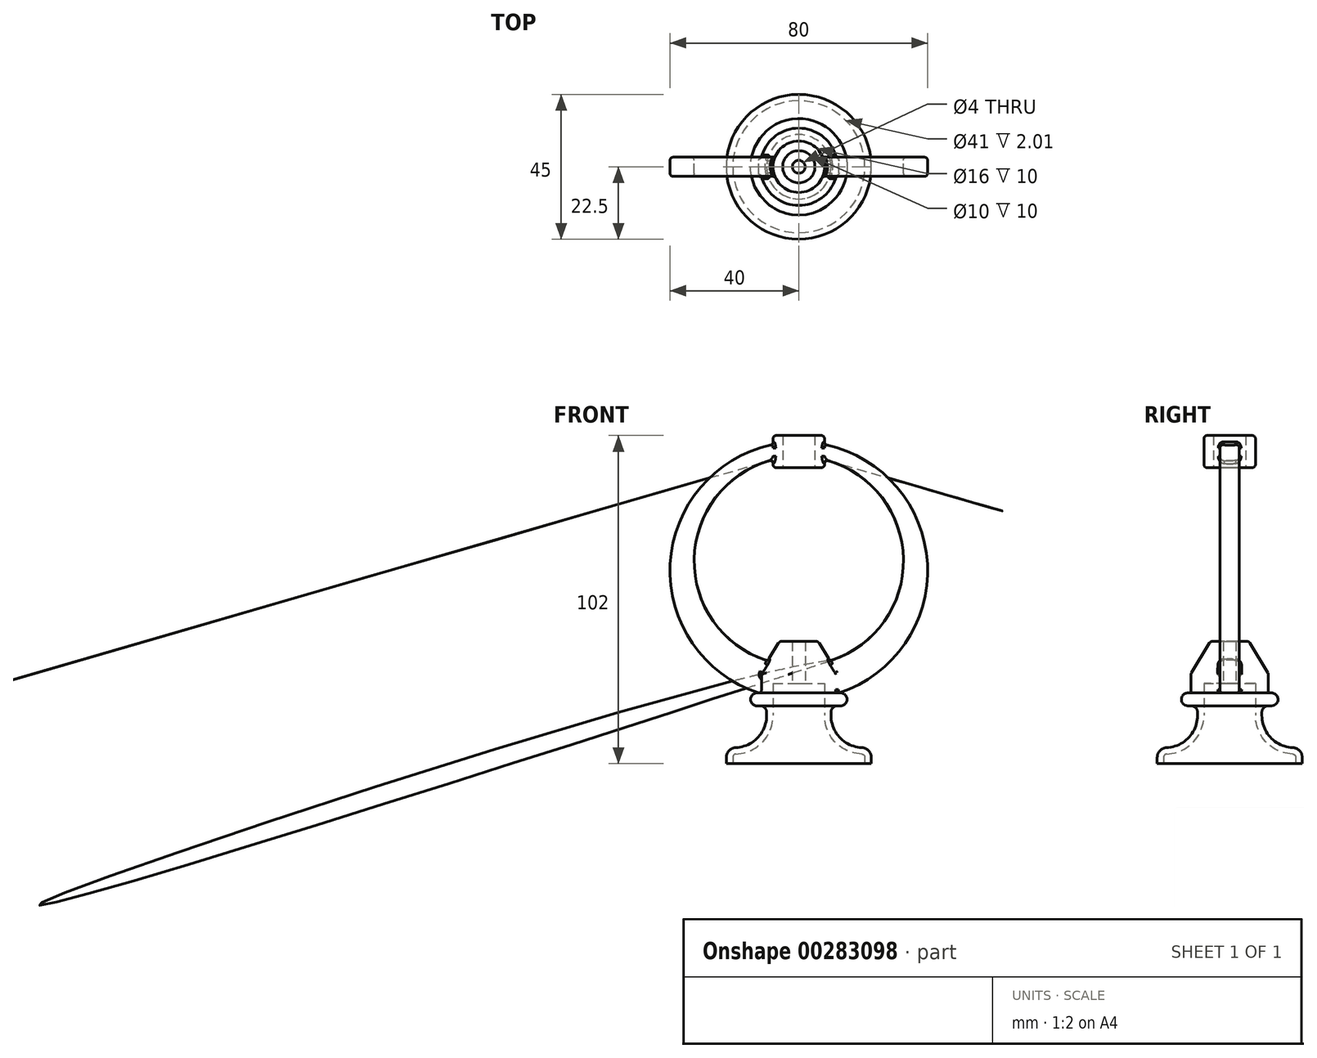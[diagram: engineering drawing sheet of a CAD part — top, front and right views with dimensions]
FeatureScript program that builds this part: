
annotation { "Feature Type Name" : "Feature", "Feature Type Description" : "" }
export const myFeature = defineFeature(function(context is Context, id is Id, definition is map)
    precondition{}
    {
        {
            var Q0;
            Q0=qCreatedBy(makeId("Front.planeOp"),FACE);
            var sketch = newSketch(context, id + "F0", { "sketchPlane" : qUnion([Q0])});
            skLineSegment(sketch, "E0", {"start": v(0, 0) * mm, "end": v(22.5, 0) * mm});
            skLineSegment(sketch, "E1", {"start": v(22.5, 0) * mm, "end": v(22.5, 5) * mm});
            skLineSegment(sketch, "E2", {"start": v(22.5, 5) * mm, "end": v(10, 5) * mm});
            skLineSegment(sketch, "E3", {"start": v(10, 5) * mm, "end": v(10, 18) * mm});
            skLineSegment(sketch, "E4", {"start": v(10, 18) * mm, "end": v(15, 18) * mm});
            skLineSegment(sketch, "E5", {"start": v(15, 18) * mm, "end": v(15, 22) * mm});
            skLineSegment(sketch, "E6", {"start": v(15, 22) * mm, "end": v(12, 22) * mm});
            skLineSegment(sketch, "E7", {"start": v(12, 22) * mm, "end": v(12, 28) * mm});
            skLineSegment(sketch, "E8", {"start": v(12, 28) * mm, "end": v(6, 38) * mm});
            skLineSegment(sketch, "E9", {"start": v(6, 38) * mm, "end": v(0, 38) * mm});
            skLineSegment(sketch, "E10", {"start": v(0, 38) * mm, "end": v(0, 0) * mm});
            skSolve(sketch);
        }
        {
            var Q0;
            Q0 = qSketchRegion(id + "F0", true);
            var Q1;
            Q1=sQuery(id+"F0.wireOp",EDGE,"E10");
            revolve(context, id + "F1", {"entities" : qUnion([Q0]), "axis" : qUnion([Q1]), "revolveType" : RevolveType.FULL});
        }
        {
            var Q0;
            Q0=qCreatedBy(makeId("Front.planeOp"),FACE);
            var sketch = newSketch(context, id + "F2", { "sketchPlane" : qUnion([Q0])});
            skCircle(sketch, "E11", {"center": v(0, 60) * mm, "radius": 40 * mm});
            skCircle(sketch, "E12", {"center": v(0, 63) * mm, "radius": 32.5 * mm});
            skSolve(sketch);
        }
        {
            var Q0;
            Q0 = qSketchRegion(id + "F2", true);
            extrude(context, id + "F3", {"entities" : qUnion([Q0]), "operationType" : NewBodyOperationType.ADD, "endBound" : BoundingType.SYMMETRIC, "depth" : 6 * mm});
        }
        {
            var Q0;
            Q0=makeQuery(id+"F1.opRevolve","SWEPT_EDGE",EDGE,{"disambiguationData":[OSD([sQuery(id+"F0.wireOp",EDGE,"E2"),sQuery(id+"F0.wireOp",EDGE,"E3")])]});
            fillet(context, id + "F4", {"entities" : qUnion([Q0]), "radius" : 10 * mm, "tangentPropagation" : true, "allowEdgeOverflow" : false});
        }
        {
            var Q0;
            Q0=makeQuery(id+"F1.opRevolve","SWEPT_EDGE",EDGE,{"disambiguationData":[OSD([sQuery(id+"F0.wireOp",EDGE,"E3"),sQuery(id+"F0.wireOp",EDGE,"E4")])]});
            var Q1;
            Q1=makeQuery(id+"F1.opRevolve","SWEPT_EDGE",EDGE,{"disambiguationData":[OSD([sQuery(id+"F0.wireOp",EDGE,"E4"),sQuery(id+"F0.wireOp",EDGE,"E5")])]});
            var Q2;
            Q2=makeQuery(id+"F1.opRevolve","SWEPT_EDGE",EDGE,{"disambiguationData":[OSD([sQuery(id+"F0.wireOp",EDGE,"E5"),sQuery(id+"F0.wireOp",EDGE,"E6")])]});
            fillet(context, id + "F5", {"entities" : qUnion([Q0, Q1, Q2]), "radius" : 2 * mm, "tangentPropagation" : true, "allowEdgeOverflow" : false});
        }
        {
            var Q0;
            Q0=makeQuery(id+"F1.opRevolve","SWEPT_EDGE",EDGE,{"disambiguationData":[OSD([sQuery(id+"F0.wireOp",EDGE,"E1"),sQuery(id+"F0.wireOp",EDGE,"E2")])]});
            fillet(context, id + "F6", {"entities" : qUnion([Q0]), "radius" : 3 * mm, "tangentPropagation" : true, "allowEdgeOverflow" : false});
        }
        {
            var Q0;
            Q0=qCreatedBy(makeId("Front.planeOp"),FACE);
            var sketch = newSketch(context, id + "F7", { "sketchPlane" : qUnion([Q0])});
            skArc(sketch, "E13", {"start": v(10, 15) * mm, "mid": v(12.8, 8.07) * mm, "end": v(19.62, 5) * mm});
            skArc(sketch, "E14", {"start": v(22.5, 2) * mm, "mid": v(21.66, 4.09) * mm, "end": v(19.62, 5) * mm});
            skLineSegment(sketch, "E15", {"start": v(22.5, 2) * mm, "end": v(22.5, 0) * mm});
            skLineSegment(sketch, "E16.0", {"start": v(20.5, 2) * mm, "end": v(20.5, 0) * mm});
            skArc(sketch, "E16.1", {"start": v(20.5, 2) * mm, "mid": v(20.22, 2.7) * mm, "end": v(19.54, 3) * mm});
            skArc(sketch, "E16.2", {"start": v(8, 15) * mm, "mid": v(11.35, 6.68) * mm, "end": v(19.54, 3) * mm});
            skLineSegment(sketch, "E17", {"start": v(8, 15) * mm, "end": v(8, 25) * mm});
            skLineSegment(sketch, "E18.0", {"start": v(-11.62, 28) * mm, "end": v(11.62, 28) * mm});
            skLineSegment(sketch, "E19", {"start": v(8, 25) * mm, "end": v(2, 25) * mm});
            skLineSegment(sketch, "E20", {"start": v(2, 25) * mm, "end": v(2, 41.12) * mm});
            skLineSegment(sketch, "E21", {"start": v(2, 41.12) * mm, "end": v(0, 41.12) * mm});
            skLineSegment(sketch, "E22", {"start": v(0, 41.12) * mm, "end": v(0, 0) * mm});
            skLineSegment(sketch, "E23", {"start": v(0, 0) * mm, "end": v(20.5, 0) * mm});
            skSolve(sketch);
        }
        {
            var Q0;
            Q0 = qSketchRegion(id + "F7", true);
            var Q1;
            Q1=sQuery(id+"F7.wireOp",EDGE,"E22");
            revolve(context, id + "F8", {"operationType" : NewBodyOperationType.REMOVE, "entities" : qUnion([Q0]), "axis" : qUnion([Q1]), "revolveType" : RevolveType.FULL, "oppositeDirection" : true});
        }
        {
            var Q0;
            Q0=qCreatedBy(makeId("Front.planeOp"),FACE);
            var sketch = newSketch(context, id + "F9", { "sketchPlane" : qUnion([Q0])});
            skLineSegment(sketch, "E24", {"start": v(0, 0) * mm, "end": v(0, 128.66) * mm, "construction": true});
            skLineSegment(sketch, "E25.bottom", {"start": v(5, 102) * mm, "end": v(8, 102) * mm});
            skLineSegment(sketch, "E25.top", {"start": v(5, 92) * mm, "end": v(8, 92) * mm});
            skLineSegment(sketch, "E25.left", {"start": v(5, 102) * mm, "end": v(5, 92) * mm});
            skLineSegment(sketch, "E25.right", {"start": v(8, 102) * mm, "end": v(8, 92) * mm});
            skSolve(sketch);
        }
        {
            var Q0;
            Q0=makeQuery(id+"F9.imprint","IMPRINT",FACE,{"disambiguationData":[TD([[makeQuery(id+"F9.imprint","IMPRINT",EDGE,{"derivedFrom":sQuery(id+"F9.wireOp",EDGE,"E25.bottom")}),-1.0]])]});
            var Q1;
            Q1=sQuery(id+"F9.wireOp",EDGE,"E24");
            revolve(context, id + "F10", {"operationType" : NewBodyOperationType.ADD, "entities" : qUnion([Q0]), "axis" : qUnion([Q1]), "revolveType" : RevolveType.FULL});
        }
        {
            var Q0;
            Q0=makeQuery(id+"F10.opRevolve","SWEPT_FACE",FACE,{"disambiguationData":[OSD([sQuery(id+"F9.wireOp",EDGE,"E25.bottom")])]});
            var sketch = newSketch(context, id + "F11", { "sketchPlane" : qUnion([Q0])});
            skCircle(sketch, "E26.0", {"center": v(0, 0) * mm, "radius": 5 * mm});
            skSolve(sketch);
        }
        {
            var Q0;
            Q0 = qSketchRegion(id + "F11", true);
            extrude(context, id + "F12", {"entities" : qUnion([Q0]), "operationType" : NewBodyOperationType.REMOVE, "oppositeDirection" : true, "depth" : 25 * mm});
        }
        {
            var Q0;
            {var subQ0=sQuery(id+"F2.wireOp",EDGE,"E12");Q0=makeQuery(id+"F10.boolean.opBoolean","SPLIT",EDGE,{"disambiguationData":[TD([makeQuery(id+"F1.opRevolve","SWEPT_FACE",FACE,{"disambiguationData":[OSD([sQuery(id+"F0.wireOp",EDGE,"E8")])]}),makeQuery(id+"F3.opExtrude","CAP_FACE",FACE,{"disambiguationData":[OSD([sQuery(id+"F2.wireOp",EDGE,"E11"),subQ0])],"isStart":false}),makeQuery(id+"F3.opExtrude","SWEPT_FACE",FACE,{"disambiguationData":[OSD([subQ0])]}),makeQuery(id+"F10.opRevolve","SWEPT_FACE",FACE,{"disambiguationData":[OSD([sQuery(id+"F9.wireOp",EDGE,"E25.right")])]})]),OD(0.0)],"derivedFrom":makeQuery(id+"F3.opExtrude","CAP_EDGE",EDGE,{"disambiguationData":[OSD([subQ0])],"isStart":false})});}
            var Q1;
            {var subQ0=sQuery(id+"F2.wireOp",EDGE,"E12");Q1=makeQuery(id+"F10.boolean.opBoolean","SPLIT",EDGE,{"disambiguationData":[TD([makeQuery(id+"F1.opRevolve","SWEPT_FACE",FACE,{"disambiguationData":[OSD([sQuery(id+"F0.wireOp",EDGE,"E8")])]}),makeQuery(id+"F3.opExtrude","CAP_FACE",FACE,{"disambiguationData":[OSD([sQuery(id+"F2.wireOp",EDGE,"E11"),subQ0])],"isStart":true}),makeQuery(id+"F3.opExtrude","SWEPT_FACE",FACE,{"disambiguationData":[OSD([subQ0])]}),makeQuery(id+"F10.opRevolve","SWEPT_FACE",FACE,{"disambiguationData":[OSD([sQuery(id+"F9.wireOp",EDGE,"E25.right")])]})]),OD(0.0)],"derivedFrom":makeQuery(id+"F3.opExtrude","CAP_EDGE",EDGE,{"disambiguationData":[OSD([subQ0])],"isStart":true})});}
            var Q2;
            {var subQ0=sQuery(id+"F2.wireOp",EDGE,"E12");Q2=makeQuery(id+"F10.boolean.opBoolean","SPLIT",EDGE,{"disambiguationData":[TD([makeQuery(id+"F1.opRevolve","SWEPT_FACE",FACE,{"disambiguationData":[OSD([sQuery(id+"F0.wireOp",EDGE,"E8")])]}),makeQuery(id+"F3.opExtrude","CAP_FACE",FACE,{"disambiguationData":[OSD([sQuery(id+"F2.wireOp",EDGE,"E11"),subQ0])],"isStart":false}),makeQuery(id+"F3.opExtrude","SWEPT_FACE",FACE,{"disambiguationData":[OSD([subQ0])]}),makeQuery(id+"F10.opRevolve","SWEPT_FACE",FACE,{"disambiguationData":[OSD([sQuery(id+"F9.wireOp",EDGE,"E25.right")])]})]),OD(1.0)],"derivedFrom":makeQuery(id+"F3.opExtrude","CAP_EDGE",EDGE,{"disambiguationData":[OSD([subQ0])],"isStart":false})});}
            var Q3;
            {var subQ0=sQuery(id+"F2.wireOp",EDGE,"E12");Q3=makeQuery(id+"F10.boolean.opBoolean","SPLIT",EDGE,{"disambiguationData":[TD([makeQuery(id+"F1.opRevolve","SWEPT_FACE",FACE,{"disambiguationData":[OSD([sQuery(id+"F0.wireOp",EDGE,"E8")])]}),makeQuery(id+"F3.opExtrude","CAP_FACE",FACE,{"disambiguationData":[OSD([sQuery(id+"F2.wireOp",EDGE,"E11"),subQ0])],"isStart":true}),makeQuery(id+"F3.opExtrude","SWEPT_FACE",FACE,{"disambiguationData":[OSD([subQ0])]}),makeQuery(id+"F10.opRevolve","SWEPT_FACE",FACE,{"disambiguationData":[OSD([sQuery(id+"F9.wireOp",EDGE,"E25.right")])]})]),OD(1.0)],"derivedFrom":makeQuery(id+"F3.opExtrude","CAP_EDGE",EDGE,{"disambiguationData":[OSD([subQ0])],"isStart":true})});}
            var Q4;
            {var subQ0=sQuery(id+"F2.wireOp",EDGE,"E11");Q4=makeQuery(id+"F10.boolean.opBoolean","SPLIT",EDGE,{"disambiguationData":[TD([makeQuery(id+"F1.opRevolve","SWEPT_FACE",FACE,{"disambiguationData":[OSD([sQuery(id+"F0.wireOp",EDGE,"E6")])]}),makeQuery(id+"F3.opExtrude","SWEPT_FACE",FACE,{"disambiguationData":[OSD([subQ0])]}),makeQuery(id+"F3.opExtrude","CAP_FACE",FACE,{"disambiguationData":[OSD([subQ0,sQuery(id+"F2.wireOp",EDGE,"E12")])],"isStart":false}),makeQuery(id+"F10.opRevolve","SWEPT_FACE",FACE,{"disambiguationData":[OSD([sQuery(id+"F9.wireOp",EDGE,"E25.right")])]})]),OD(1.0)],"derivedFrom":makeQuery(id+"F3.opExtrude","CAP_EDGE",EDGE,{"disambiguationData":[OSD([subQ0])],"isStart":false})});}
            var Q5;
            {var subQ0=sQuery(id+"F2.wireOp",EDGE,"E11");Q5=makeQuery(id+"F10.boolean.opBoolean","SPLIT",EDGE,{"disambiguationData":[TD([makeQuery(id+"F1.opRevolve","SWEPT_FACE",FACE,{"disambiguationData":[OSD([sQuery(id+"F0.wireOp",EDGE,"E6")])]}),makeQuery(id+"F3.opExtrude","SWEPT_FACE",FACE,{"disambiguationData":[OSD([subQ0])]}),makeQuery(id+"F3.opExtrude","CAP_FACE",FACE,{"disambiguationData":[OSD([subQ0,sQuery(id+"F2.wireOp",EDGE,"E12")])],"isStart":false}),makeQuery(id+"F10.opRevolve","SWEPT_FACE",FACE,{"disambiguationData":[OSD([sQuery(id+"F9.wireOp",EDGE,"E25.right")])]})]),OD(0.0)],"derivedFrom":makeQuery(id+"F3.opExtrude","CAP_EDGE",EDGE,{"disambiguationData":[OSD([subQ0])],"isStart":false})});}
            var Q6;
            {var subQ0=sQuery(id+"F2.wireOp",EDGE,"E11");Q6=makeQuery(id+"F10.boolean.opBoolean","SPLIT",EDGE,{"disambiguationData":[TD([makeQuery(id+"F1.opRevolve","SWEPT_FACE",FACE,{"disambiguationData":[OSD([sQuery(id+"F0.wireOp",EDGE,"E6")])]}),makeQuery(id+"F3.opExtrude","SWEPT_FACE",FACE,{"disambiguationData":[OSD([subQ0])]}),makeQuery(id+"F3.opExtrude","CAP_FACE",FACE,{"disambiguationData":[OSD([subQ0,sQuery(id+"F2.wireOp",EDGE,"E12")])],"isStart":true}),makeQuery(id+"F10.opRevolve","SWEPT_FACE",FACE,{"disambiguationData":[OSD([sQuery(id+"F9.wireOp",EDGE,"E25.right")])]})]),OD(1.0)],"derivedFrom":makeQuery(id+"F3.opExtrude","CAP_EDGE",EDGE,{"disambiguationData":[OSD([subQ0])],"isStart":true})});}
            var Q7;
            {var subQ0=sQuery(id+"F2.wireOp",EDGE,"E11");Q7=makeQuery(id+"F10.boolean.opBoolean","SPLIT",EDGE,{"disambiguationData":[TD([makeQuery(id+"F1.opRevolve","SWEPT_FACE",FACE,{"disambiguationData":[OSD([sQuery(id+"F0.wireOp",EDGE,"E6")])]}),makeQuery(id+"F3.opExtrude","SWEPT_FACE",FACE,{"disambiguationData":[OSD([subQ0])]}),makeQuery(id+"F3.opExtrude","CAP_FACE",FACE,{"disambiguationData":[OSD([subQ0,sQuery(id+"F2.wireOp",EDGE,"E12")])],"isStart":true}),makeQuery(id+"F10.opRevolve","SWEPT_FACE",FACE,{"disambiguationData":[OSD([sQuery(id+"F9.wireOp",EDGE,"E25.right")])]})]),OD(0.0)],"derivedFrom":makeQuery(id+"F3.opExtrude","CAP_EDGE",EDGE,{"disambiguationData":[OSD([subQ0])],"isStart":true})});}
            var Q8;
            Q8=makeQuery(id+"F10.opRevolve","SWEPT_EDGE",EDGE,{"disambiguationData":[OSD([sQuery(id+"F9.wireOp",EDGE,"E25.bottom"),sQuery(id+"F9.wireOp",EDGE,"E25.right")])]});
            var Q9;
            Q9=makeQuery(id+"F10.opRevolve","SWEPT_EDGE",EDGE,{"disambiguationData":[OSD([sQuery(id+"F9.wireOp",EDGE,"E25.top"),sQuery(id+"F9.wireOp",EDGE,"E25.right")])]});
            fillet(context, id + "F13", {"entities" : qUnion([Q0, Q1, Q2, Q3, Q4, Q5, Q6, Q7, Q8, Q9]), "radius" : 1 * mm, "tangentPropagation" : true, "allowEdgeOverflow" : false});
        }
        {
            var Q0;
            {var subQ0=makeQuery(id+"F10.opRevolve","SWEPT_FACE",FACE,{"disambiguationData":[OSD([sQuery(id+"F9.wireOp",EDGE,"E25.right")])]});var subQ1=sQuery(id+"F2.wireOp",EDGE,"E11");Q0=makeQuery(id+"F13.opFillet","BLEND_EDGE",EDGE,{"blendedFrom":[makeQuery(id+"F10.boolean.opBoolean","SPLIT",EDGE,{"disambiguationData":[TD([makeQuery(id+"F1.opRevolve","SWEPT_FACE",FACE,{"disambiguationData":[OSD([sQuery(id+"F0.wireOp",EDGE,"E6")])]}),makeQuery(id+"F3.opExtrude","SWEPT_FACE",FACE,{"disambiguationData":[OSD([subQ1])]}),makeQuery(id+"F3.opExtrude","CAP_FACE",FACE,{"disambiguationData":[OSD([subQ1,sQuery(id+"F2.wireOp",EDGE,"E12")])],"isStart":true}),subQ0]),OD(0.0)],"derivedFrom":makeQuery(id+"F3.opExtrude","CAP_EDGE",EDGE,{"disambiguationData":[OSD([subQ1])],"isStart":true})}),subQ0],"blendedInto":[subQ0]});}
            var Q1;
            Q1=makeQuery(id+"F10.boolean.opBoolean","INTERSECT",EDGE,{"disambiguationData":[OD(1.0)],"derivedFrom":[makeQuery(id+"F3.opExtrude","CAP_FACE",FACE,{"disambiguationData":[OSD([sQuery(id+"F2.wireOp",EDGE,"E11"),sQuery(id+"F2.wireOp",EDGE,"E12")])],"isStart":true}),makeQuery(id+"F10.opRevolve","SWEPT_FACE",FACE,{"disambiguationData":[OSD([sQuery(id+"F9.wireOp",EDGE,"E25.right")])]})]});
            var Q2;
            Q2=makeQuery(id+"F3.boolean.opBoolean","INTERSECT",EDGE,{"disambiguationData":[OD(1.0)],"derivedFrom":[makeQuery(id+"F1.opRevolve","SWEPT_FACE",FACE,{"disambiguationData":[OSD([sQuery(id+"F0.wireOp",EDGE,"E7")])]}),makeQuery(id+"F3.opExtrude","CAP_FACE",FACE,{"disambiguationData":[OSD([sQuery(id+"F2.wireOp",EDGE,"E11"),sQuery(id+"F2.wireOp",EDGE,"E12")])],"isStart":true})]});
            var Q3;
            Q3=makeQuery(id+"F3.boolean.opBoolean","INTERSECT",EDGE,{"disambiguationData":[OD(1.0)],"derivedFrom":[makeQuery(id+"F1.opRevolve","SWEPT_FACE",FACE,{"disambiguationData":[OSD([sQuery(id+"F0.wireOp",EDGE,"E8")])]}),makeQuery(id+"F3.opExtrude","CAP_FACE",FACE,{"disambiguationData":[OSD([sQuery(id+"F2.wireOp",EDGE,"E11"),sQuery(id+"F2.wireOp",EDGE,"E12")])],"isStart":true})]});
            var Q4;
            Q4=makeQuery(id+"F3.boolean.opBoolean","INTERSECT",EDGE,{"disambiguationData":[OD(1.0)],"derivedFrom":[makeQuery(id+"F1.opRevolve","SWEPT_FACE",FACE,{"disambiguationData":[OSD([sQuery(id+"F0.wireOp",EDGE,"E7")])]}),makeQuery(id+"F3.opExtrude","CAP_FACE",FACE,{"disambiguationData":[OSD([sQuery(id+"F2.wireOp",EDGE,"E11"),sQuery(id+"F2.wireOp",EDGE,"E12")])],"isStart":false})]});
            var Q5;
            Q5=makeQuery(id+"F1.opRevolve","SWEPT_FACE",FACE,{"disambiguationData":[OSD([sQuery(id+"F0.wireOp",EDGE,"E8")])]});
            fillet(context, id + "F14", {"entities" : qUnion([Q0, Q1, Q2, Q3, Q4, Q5]), "radius" : 1 * mm, "tangentPropagation" : true, "allowEdgeOverflow" : false});
        }
    });
